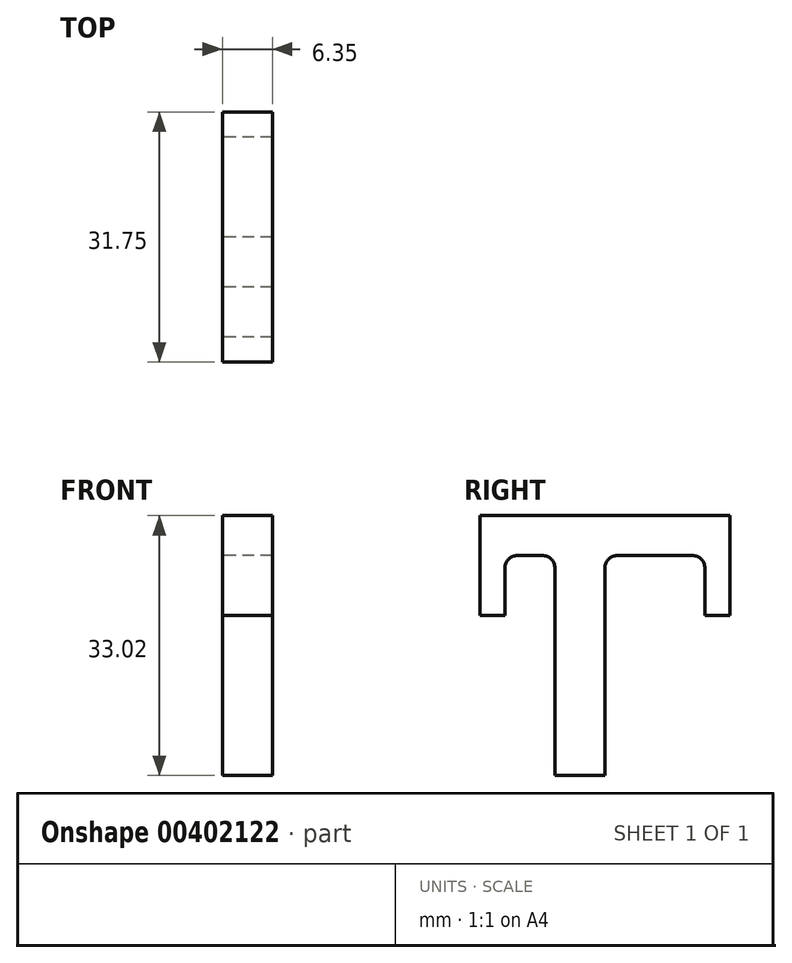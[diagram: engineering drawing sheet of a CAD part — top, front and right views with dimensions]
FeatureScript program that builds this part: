
annotation { "Feature Type Name" : "Feature", "Feature Type Description" : "" }
export const myFeature = defineFeature(function(context is Context, id is Id, definition is map)
    precondition{}
    {
        {
            var Q0;
            Q0=qCreatedBy(makeId("Right.planeOp"),FACE);
            var sketch = newSketch(context, id + "F0", { "sketchPlane" : qUnion([Q0])});
            skLineSegment(sketch, "E0.bottom", {"start": v(-3.18, 16.51) * mm, "end": v(3.17, 16.51) * mm});
            skLineSegment(sketch, "E0.top", {"start": v(-3.17, -16.51) * mm, "end": v(3.18, -16.51) * mm});
            skLineSegment(sketch, "E0.left", {"start": v(-3.18, 9.84) * mm, "end": v(-3.17, -16.51) * mm});
            skLineSegment(sketch, "E0.right", {"start": v(3.17, 9.84) * mm, "end": v(3.18, -16.51) * mm});
            skPoint(sketch, "E0.middle", {"position": v(0, 0) * mm});
            skLineSegment(sketch, "E1.bottom", {"start": v(-9.53, 16.51) * mm, "end": v(15.87, 16.51) * mm});
            skLineSegment(sketch, "E1.top", {"start": v(-7.94, 11.43) * mm, "end": v(-4.76, 11.43) * mm});
            skLineSegment(sketch, "E2.bottom", {"start": v(-9.53, 16.51) * mm, "end": v(-12.7, 16.5) * mm});
            skLineSegment(sketch, "E2.top", {"start": v(-9.53, 3.8) * mm, "end": v(-12.7, 3.8) * mm});
            skLineSegment(sketch, "E2.left", {"start": v(-9.53, 9.84) * mm, "end": v(-9.53, 3.8) * mm});
            skLineSegment(sketch, "E2.right", {"start": v(-12.7, 16.5) * mm, "end": v(-12.7, 3.8) * mm});
            skLineSegment(sketch, "E3.bottom", {"start": v(15.87, 16.51) * mm, "end": v(19.05, 16.51) * mm});
            skLineSegment(sketch, "E3.top", {"start": v(15.87, 3.81) * mm, "end": v(19.05, 3.81) * mm});
            skLineSegment(sketch, "E3.left", {"start": v(15.87, 9.84) * mm, "end": v(15.87, 3.81) * mm});
            skLineSegment(sketch, "E3.right", {"start": v(19.05, 16.51) * mm, "end": v(19.05, 3.81) * mm});
            skLineSegment(sketch, "E4.bottom", {"start": v(-11.7, -0.8) * mm, "end": v(-5.35, -0.8) * mm});
            skLineSegment(sketch, "E4.top", {"start": v(-11.7, -7.15) * mm, "end": v(-5.35, -7.15) * mm});
            skLineSegment(sketch, "E4.left", {"start": v(-11.7, -0.8) * mm, "end": v(-11.7, -7.15) * mm});
            skLineSegment(sketch, "E4.right", {"start": v(-5.35, -0.8) * mm, "end": v(-5.35, -7.15) * mm});
            skLineSegment(sketch, "E5.trimOffspring", {"start": v(4.76, 11.43) * mm, "end": v(14.29, 11.43) * mm});
            skPoint(sketch, "E6.visualSharp", {"position": v(-9.53, 11.43) * mm});
            skArc(sketch, "E6.filletArc", {"start": v(-7.94, 11.43) * mm, "mid": v(-9.06, 10.97) * mm, "end": v(-9.53, 9.84) * mm});
            skPoint(sketch, "E7.visualSharp", {"position": v(-3.18, 11.43) * mm});
            skArc(sketch, "E7.filletArc", {"start": v(-3.18, 9.84) * mm, "mid": v(-3.64, 10.97) * mm, "end": v(-4.76, 11.43) * mm});
            skPoint(sketch, "E8.visualSharp", {"position": v(3.17, 11.43) * mm});
            skArc(sketch, "E8.filletArc", {"start": v(4.76, 11.43) * mm, "mid": v(3.64, 10.97) * mm, "end": v(3.17, 9.84) * mm});
            skPoint(sketch, "E9.visualSharp", {"position": v(15.87, 11.43) * mm});
            skArc(sketch, "E9.filletArc", {"start": v(15.87, 9.84) * mm, "mid": v(15.41, 10.97) * mm, "end": v(14.29, 11.43) * mm});
            skLineSegment(sketch, "E10.bottom", {"start": v(5.76, -6.2) * mm, "end": v(12.1, -6.2) * mm});
            skLineSegment(sketch, "E10.top", {"start": v(5.76, -12.56) * mm, "end": v(12.1, -12.56) * mm});
            skLineSegment(sketch, "E10.left", {"start": v(5.76, -6.2) * mm, "end": v(5.76, -12.56) * mm});
            skLineSegment(sketch, "E10.right", {"start": v(12.1, -6.2) * mm, "end": v(12.1, -12.56) * mm});
            skLineSegment(sketch, "E11", {"start": v(-3.18, 3.81) * mm, "end": v(3.17, 3.81) * mm, "construction": true});
            skSolve(sketch);
        }
        {
            var Q0;
            Q0=makeQuery(id+"F0.imprint","IMPRINT",FACE,{"disambiguationData":[TD([[makeQuery(id+"F0.imprint","IMPRINT",EDGE,{"derivedFrom":sQuery(id+"F0.wireOp",EDGE,"E1.top")}),1.0]])]});
            var Q1;
            {var subQ0=sQuery(id+"F0.wireOp",EDGE,"E0.top");Q1=makeQuery(id+"F0.imprint","IMPRINT",FACE,{"disambiguationData":[TD([[makeQuery(id+"F0.imprint","IMPRINT",EDGE,{"derivedFrom":subQ0}),1.0]])]});}
            extrude(context, id + "F1", {"entities" : qUnion([Q0, Q1]), "depth" : 6.35 * mm});
        }
    });
